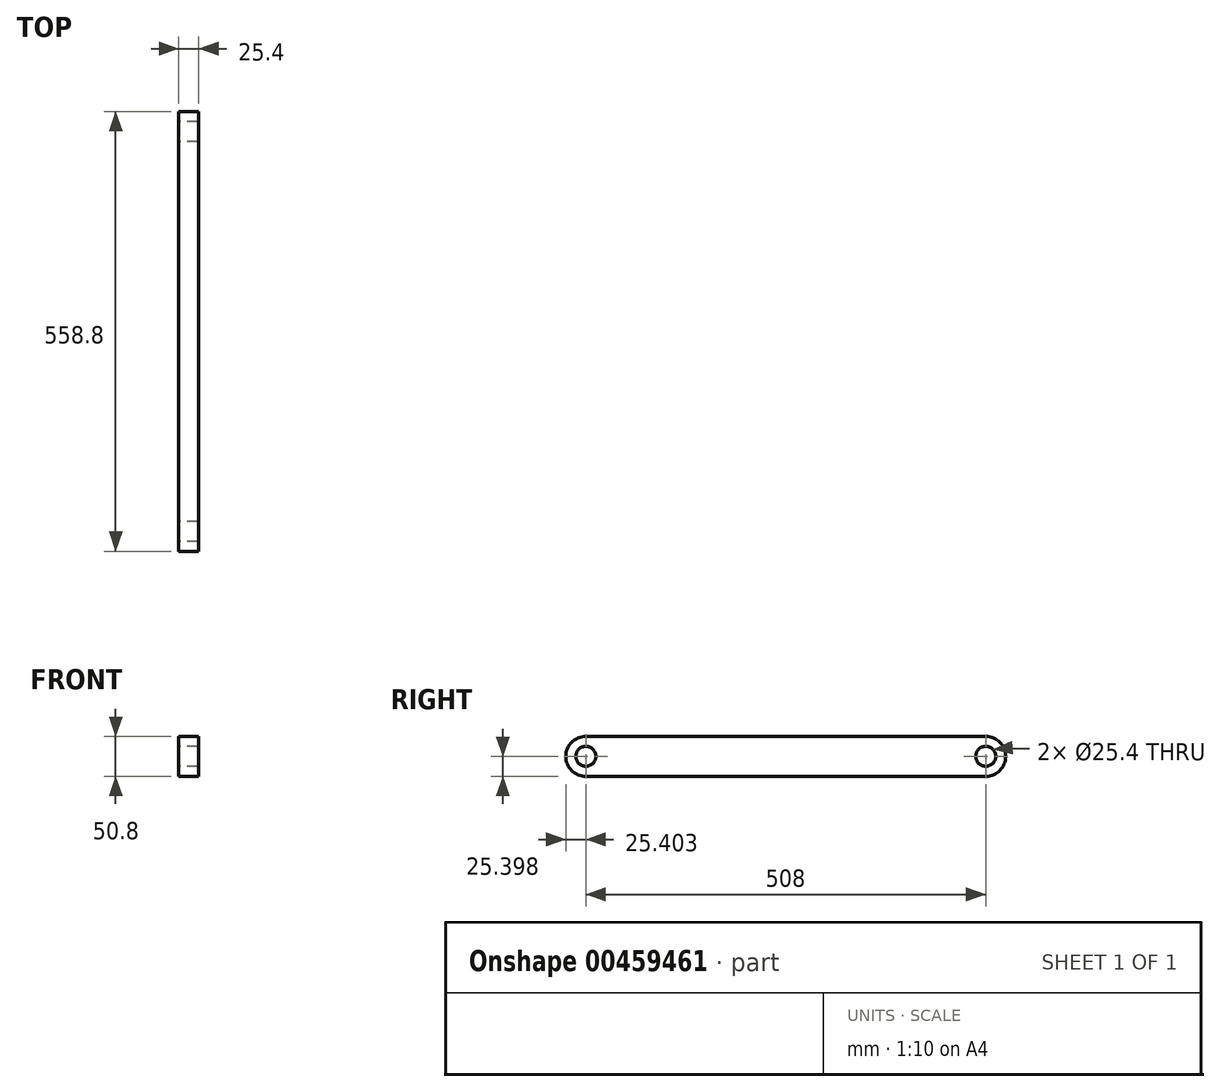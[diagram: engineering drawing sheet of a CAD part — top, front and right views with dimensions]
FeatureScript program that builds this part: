
annotation { "Feature Type Name" : "Feature", "Feature Type Description" : "" }
export const myFeature = defineFeature(function(context is Context, id is Id, definition is map)
    precondition{}
    {
        {
            var Q0;
            Q0=qCreatedBy(makeId("Right.planeOp"),FACE);
            var sketch = newSketch(context, id + "F0", { "sketchPlane" : qUnion([Q0])});
            skLineSegment(sketch, "E0.bottom", {"start": v(-116.88, 13.44) * mm, "end": v(391.12, 13.44) * mm});
            skLineSegment(sketch, "E0.top", {"start": v(-116.88, -37.36) * mm, "end": v(391.12, -37.36) * mm});
            skLineSegment(sketch, "E0.left", {"start": v(-116.88, 13.44) * mm, "end": v(-116.88, -37.36) * mm});
            skLineSegment(sketch, "E0.right", {"start": v(391.12, 13.44) * mm, "end": v(391.12, -37.36) * mm});
            skCircle(sketch, "E1", {"center": v(-116.88, -11.96) * mm, "radius": 25.4 * mm});
            skCircle(sketch, "E2", {"center": v(391.12, -11.96) * mm, "radius": 25.4 * mm});
            skCircle(sketch, "E3", {"center": v(391.12, -11.96) * mm, "radius": 12.7 * mm});
            skCircle(sketch, "E4", {"center": v(-116.88, -11.96) * mm, "radius": 12.7 * mm});
            skSolve(sketch);
        }
        {
            var Q0;
            Q0=qSketchRegion(id+"F0",true);
            extrude(context, id + "F1", {"entities" : qUnion([Q0]), "depth" : 25.4 * mm});
        }
    });
